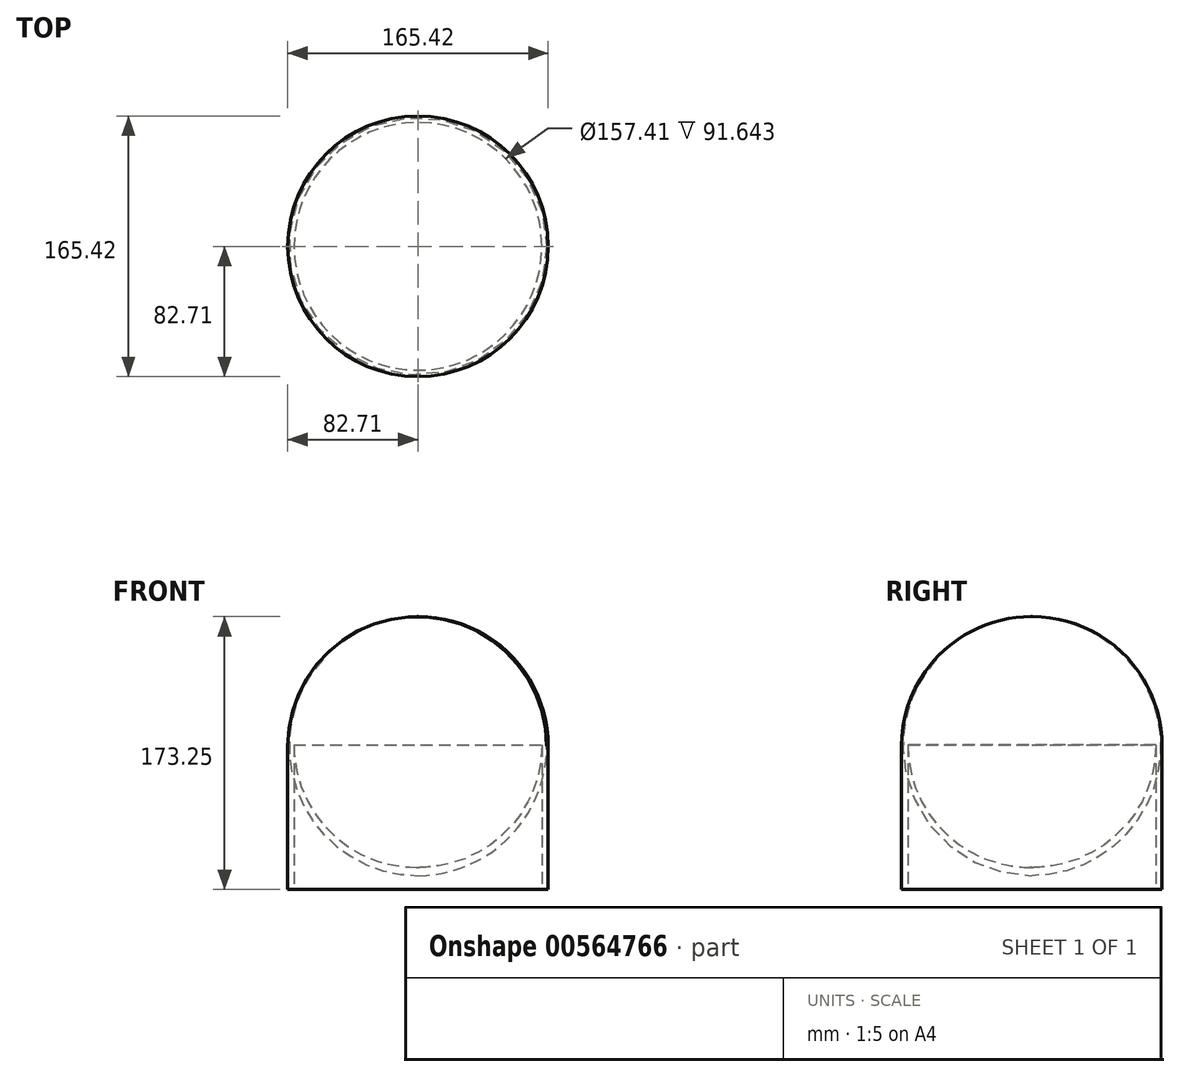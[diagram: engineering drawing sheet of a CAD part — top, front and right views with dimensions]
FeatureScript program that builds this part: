
annotation { "Feature Type Name" : "Feature", "Feature Type Description" : "" }
export const myFeature = defineFeature(function(context is Context, id is Id, definition is map)
    precondition{}
    {
        {
            var Q0;
            Q0=qCreatedBy(makeId("Front.planeOp"),FACE);
            var sketch = newSketch(context, id + "F0", { "sketchPlane" : qUnion([Q0])});
            skLineSegment(sketch, "E0", {"start": v(82.7, -86.22) * mm, "end": v(82.7, 4.78) * mm});
            skLineSegment(sketch, "E1", {"start": v(82.7, -86.22) * mm, "end": v(78.7, -86.22) * mm});
            skLineSegment(sketch, "E2", {"start": v(78.7, -86.22) * mm, "end": v(78.7, 5.43) * mm});
            skLineSegment(sketch, "E3", {"start": v(0, 83.03) * mm, "end": v(0, 87.03) * mm});
            skArc(sketch, "E4", {"start": v(78.7, 5.43) * mm, "mid": v(55.59, 60.7) * mm, "end": v(0, 83.03) * mm});
            skArc(sketch, "E5", {"start": v(82.7, 4.78) * mm, "mid": v(58.45, 63.1) * mm, "end": v(0, 87.03) * mm});
            skSolve(sketch);
        }
        {
            var Q0;
            Q0=makeQuery(id+"F0.imprint","IMPRINT",FACE,{"disambiguationData":[TD([[makeQuery(id+"F0.imprint","IMPRINT",EDGE,{"derivedFrom":sQuery(id+"F0.wireOp",EDGE,"E0")}),1.0]])]});
            var Q1;
            Q1=sQuery(id+"F0.wireOp",EDGE,"E3");
            revolve(context, id + "F1", {"entities" : qUnion([Q0]), "axis" : qUnion([Q1]), "revolveType" : RevolveType.FULL});
        }
    });
